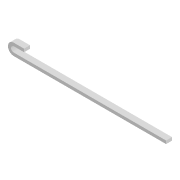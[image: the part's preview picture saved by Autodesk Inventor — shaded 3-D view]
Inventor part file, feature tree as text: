
AUTODESK INVENTOR PART (.ipt)
format: ipt  version: 2020 (Build 240168000, 168)  size: 85,504 bytes
history: native  units: mm
features: extrude x1, sketch x1
ambient origin geometry x8: Origin, YZ Plane, XZ Plane, XY Plane, X Axis, Y Axis, Z Axis, Center Point
bodies: Solid1 (feature_tree)
feature tree (2):
  extrude  "Extrusion1"  Depth=20.0mm
  sketch  "Sketch1"  dims[d0=76.0mm d1=20.0mm d2=20.0mm d4=1000.0mm d5=39.0mm d6=0.0mm d7=68.0mm]
